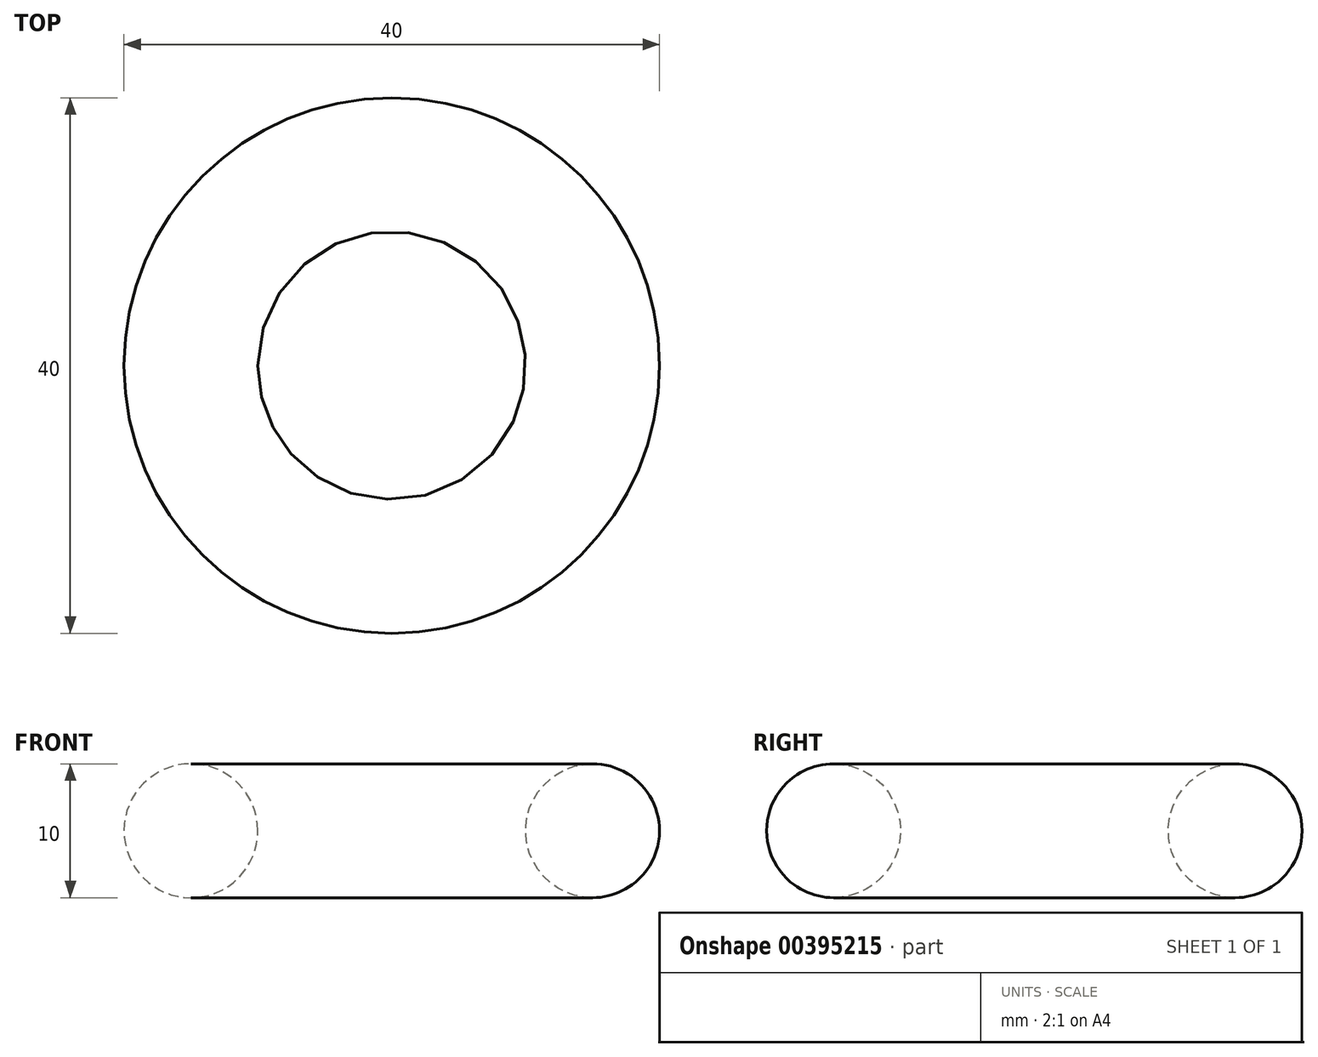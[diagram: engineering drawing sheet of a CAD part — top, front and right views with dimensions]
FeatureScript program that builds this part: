
annotation { "Feature Type Name" : "Feature", "Feature Type Description" : "" }
export const myFeature = defineFeature(function(context is Context, id is Id, definition is map)
    precondition{}
    {
        {
            var Q0;
            Q0=qCreatedBy(makeId("Right.planeOp"),FACE);
            var sketch = newSketch(context, id + "F0", { "sketchPlane" : qUnion([Q0])});
            skLineSegment(sketch, "E0", {"start": v(0, 0) * mm, "end": v(0, 8.63) * mm});
            skSolve(sketch);
        }
        {
            var Q0;
            Q0=qCreatedBy(makeId("Front.planeOp"),FACE);
            var sketch = newSketch(context, id + "F1", { "sketchPlane" : qUnion([Q0])});
            skLineSegment(sketch, "E1.bottom", {"start": v(0, 0) * mm, "end": v(15, 0) * mm});
            skLineSegment(sketch, "E1.top", {"start": v(0, -10) * mm, "end": v(15, -10) * mm});
            skLineSegment(sketch, "E1.left", {"start": v(0, 0) * mm, "end": v(0, -10) * mm});
            skLineSegment(sketch, "E1.right", {"start": v(15, 0) * mm, "end": v(15, -10) * mm});
            skCircle(sketch, "E2", {"center": v(15, -5) * mm, "radius": 5 * mm});
            skSolve(sketch);
        }
        {
            var Q0;
            {var subQ0=sQuery(id+"F1.wireOp",EDGE,"E1.right");Q0=makeQuery(id+"F1.imprint","IMPRINT",FACE,{"disambiguationData":[TD([[makeQuery(id+"F1.imprint","IMPRINT",EDGE,{"derivedFrom":subQ0}),-1.0]])]});}
            var Q1;
            {var subQ0=sQuery(id+"F1.wireOp",EDGE,"E1.right");Q1=makeQuery(id+"F1.imprint","IMPRINT",FACE,{"disambiguationData":[TD([[makeQuery(id+"F1.imprint","IMPRINT",EDGE,{"derivedFrom":subQ0}),1.0]])]});}
            var Q2;
            Q2=sQuery(id+"F0.wireOp",EDGE,"E0");
            revolve(context, id + "F2", {"entities" : qUnion([Q0, Q1]), "axis" : qUnion([Q2]), "revolveType" : RevolveType.FULL});
        }
    });
